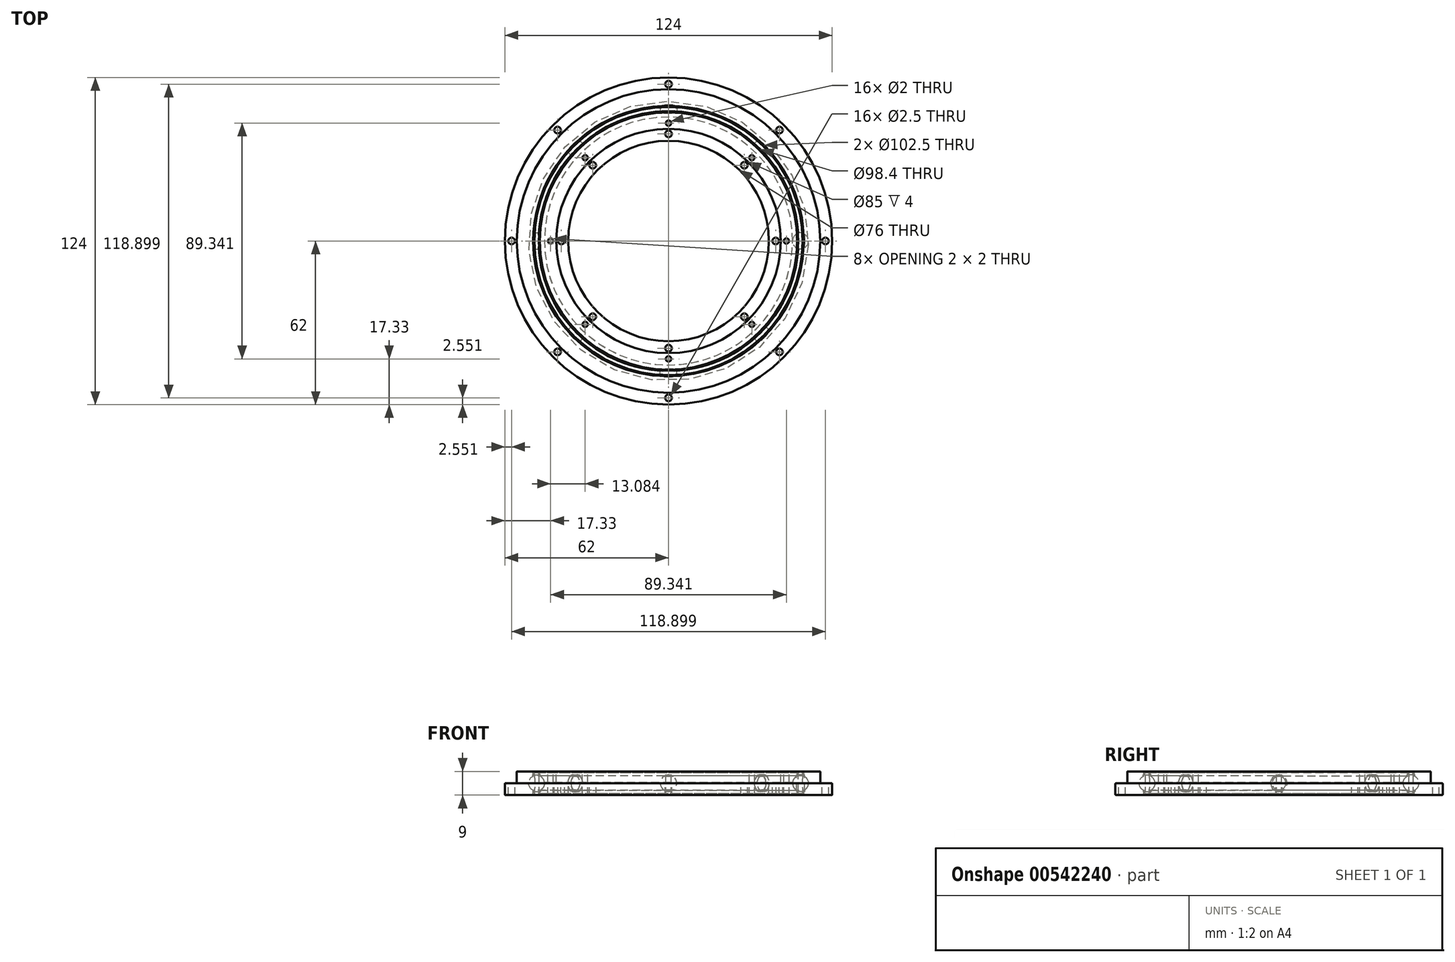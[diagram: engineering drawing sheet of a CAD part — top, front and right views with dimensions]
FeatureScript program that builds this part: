
annotation { "Feature Type Name" : "Feature", "Feature Type Description" : "" }
export const myFeature = defineFeature(function(context is Context, id is Id, definition is map)
    precondition{}
    {
        {
            var Q0;
            Q0=qCreatedBy(makeId("Front.planeOp"),FACE);
            var sketch = newSketch(context, id + "F0", { "sketchPlane" : qUnion([Q0])});
            skLineSegment(sketch, "E0", {"start": v(0, 5.1) * mm, "end": v(0, -5.34) * mm, "construction": true});
            skLineSegment(sketch, "E1", {"start": v(-106.53, 0) * mm, "end": v(60.8, 0) * mm, "construction": true});
            skLineSegment(sketch, "E2", {"start": v(50, 13.16) * mm, "end": v(50, -12.43) * mm, "construction": true});
            skCircle(sketch, "E3", {"center": v(50, 0) * mm, "radius": 3 * mm, "construction": true});
            skArc(sketch, "E4", {"start": v(51.25, 2.73) * mm, "mid": v(53, 0) * mm, "end": v(51.25, -2.73) * mm});
            skArc(sketch, "E5", {"start": v(48.75, 2.73) * mm, "mid": v(47, 0) * mm, "end": v(48.75, -2.73) * mm});
            skLineSegment(sketch, "E6", {"start": v(47.01, 0.25) * mm, "end": v(42.5, 0.25) * mm});
            skLineSegment(sketch, "E7", {"start": v(42.5, 0.25) * mm, "end": v(42.5, 4.5) * mm});
            skLineSegment(sketch, "E8", {"start": v(42.5, 4.5) * mm, "end": v(48.75, 4.5) * mm});
            skLineSegment(sketch, "E9", {"start": v(48.75, 4.5) * mm, "end": v(48.75, 2.73) * mm});
            skLineSegment(sketch, "E10", {"start": v(47, 0) * mm, "end": v(38, 0) * mm});
            skLineSegment(sketch, "E11", {"start": v(38, 0) * mm, "end": v(38, -4.5) * mm});
            skLineSegment(sketch, "E12", {"start": v(38, -4.5) * mm, "end": v(48.75, -4.5) * mm});
            skLineSegment(sketch, "E13", {"start": v(48.75, -4.5) * mm, "end": v(48.75, -2.73) * mm});
            skLineSegment(sketch, "E14", {"start": v(51.25, -2.73) * mm, "end": v(51.25, -4.5) * mm});
            skLineSegment(sketch, "E15", {"start": v(51.25, -4.5) * mm, "end": v(62, -4.5) * mm});
            skLineSegment(sketch, "E16", {"start": v(57.5, 0) * mm, "end": v(57.5, 4.5) * mm});
            skLineSegment(sketch, "E17", {"start": v(57.5, 4.5) * mm, "end": v(51.25, 4.5) * mm});
            skLineSegment(sketch, "E18", {"start": v(51.25, 4.5) * mm, "end": v(51.25, 2.73) * mm});
            skLineSegment(sketch, "E19", {"start": v(49.2, 4) * mm, "end": v(49.2, -4) * mm});
            skLineSegment(sketch, "E20", {"start": v(49.2, -4) * mm, "end": v(50.8, -4) * mm});
            skLineSegment(sketch, "E21", {"start": v(50.8, -4) * mm, "end": v(50.8, 4) * mm});
            skLineSegment(sketch, "E22", {"start": v(50.8, 4) * mm, "end": v(49.2, 4) * mm});
            skLineSegment(sketch, "E23", {"start": v(57.5, 0) * mm, "end": v(62, 0) * mm});
            skLineSegment(sketch, "E24", {"start": v(62, 0) * mm, "end": v(62, -4.5) * mm});
            skSolve(sketch);
        }
        {
            var Q0;
            Q0 = qSketchRegion(id + "F0", true);
            var Q1;
            Q1=sQuery(id+"F0.wireOp",EDGE,"E0");
            revolve(context, id + "F1", {"surfaceOperationType" : NewSurfaceOperationType.NEW, "entities" : qUnion([Q0]), "axis" : qUnion([Q1]), "revolveType" : RevolveType.FULL});
        }
        {
            var Q0;
            Q0=qCreatedBy(makeId("Front.planeOp"),FACE);
            var sketch = newSketch(context, id + "F2", { "sketchPlane" : qUnion([Q0])});
            skArc(sketch, "E25", {"start": v(50, 3) * mm, "mid": v(53, 0) * mm, "end": v(50, -3) * mm});
            skLineSegment(sketch, "E26", {"start": v(50, 3) * mm, "end": v(50, -3) * mm});
            skSolve(sketch);
        }
        {
            var Q0;
            Q0 = qSketchRegion(id + "F2", true);
            var Q1;
            Q1=sQuery(id+"F2.wireOp",EDGE,"E26");
            revolve(context, id + "F3", {"surfaceOperationType" : NewSurfaceOperationType.NEW, "entities" : qUnion([Q0]), "axis" : qUnion([Q1]), "revolveType" : RevolveType.FULL});
        }
        {
            assignVariable(context, id + "F4", {"name" : "num_balls", "anyValue" : 8});
        }
        {
            var Q0;
            Q0=qCreatedBy(makeId("Right.planeOp"),FACE);
            var Q1;
            Q1=sQuery(id+"F0.wireOp",VERTEX,"E3.center");
            cPlane(context, id + "F5", {"entities" : qUnion([Q0, Q1]), "cplaneType" : CPlaneType.PLANE_POINT, "offset" : 25 * mm, "width" : 150 * mm, "height" : 150 * mm});
        }
        {
            var Q0;
            Q0=qCreatedBy(id+"F5.planeOp",FACE);
            var sketch = newSketch(context, id + "F6", { "sketchPlane" : qUnion([Q0])});
            skCircle(sketch, "E27", {"center": v(0, 0) * mm, "radius": 3.12 * mm});
            skSolve(sketch);
        }
        {
            var Q0;
            Q0 = qSketchRegion(id + "F6", true);
            extrude(context, id + "F7", {"entities" : qUnion([Q0]), "endBound" : BoundingType.SYMMETRIC, "depth" : 3 * mm, "offsetDistance" : 25 * mm});
        }
        {
            var Q0;
            Q0=makeQuery(id+"F7.opExtrude","SWEPT_BODY",BODY,{"disambiguationData":[OSD([sQuery(id+"F6.wireOp",EDGE,"E27")])]});
            var Q1;
            Q1=sQuery(id+"F0.wireOp",EDGE,"E0");
            circularPattern(context, id + "F8", {"operationType" : NewBodyOperationType.REMOVE, "entities" : qUnion([Q0]), "axis" : qUnion([Q1]), "angle" : 360 * degree, "instanceCount" : getVariable(context, 'num_balls'), "equalSpace" : true});
        }
        {
            var Q0;
            Q0=makeQuery(id+"F1.opRevolve","SWEPT_FACE",FACE,{"disambiguationData":[OSD([sQuery(id+"F0.wireOp",EDGE,"E8")])]});
            var sketch = newSketch(context, id + "F9", { "sketchPlane" : qUnion([Q0])});
            skCircle(sketch, "E28", {"center": v(44.67, 0) * mm, "radius": 1 * mm});
            skCircle(sketch, "E29", {"center": v(40.6, 0) * mm, "radius": 1.25 * mm});
            skCircle(sketch, "E30", {"center": v(59.45, 0) * mm, "radius": 1.25 * mm});
            skCircle(sketch, "E31.1.0", {"center": v(28.71, 28.71) * mm, "radius": 1.25 * mm});
            skCircle(sketch, "E31.1.1", {"center": v(31.59, 31.59) * mm, "radius": 1 * mm});
            skCircle(sketch, "E31.1.2", {"center": v(42.04, 42.04) * mm, "radius": 1.25 * mm});
            skCircle(sketch, "E31.2.0", {"center": v(0, 40.6) * mm, "radius": 1.25 * mm});
            skCircle(sketch, "E31.2.1", {"center": v(0, 44.67) * mm, "radius": 1 * mm});
            skCircle(sketch, "E31.2.2", {"center": v(0, 59.45) * mm, "radius": 1.25 * mm});
            skPoint(sketch, "E31.center", {"position": v(0, 0) * mm});
            skCircle(sketch, "E32.1.3.0", {"center": v(-28.71, 28.71) * mm, "radius": 1.25 * mm});
            skCircle(sketch, "E32.2.3.0", {"center": v(-31.59, 31.59) * mm, "radius": 1 * mm});
            skCircle(sketch, "E32.4.3.0", {"center": v(-42.04, 42.04) * mm, "radius": 1.25 * mm});
            skCircle(sketch, "E32.1.4.0", {"center": v(-40.6, 0) * mm, "radius": 1.25 * mm});
            skCircle(sketch, "E32.2.4.0", {"center": v(-44.67, 0) * mm, "radius": 1 * mm});
            skCircle(sketch, "E32.4.4.0", {"center": v(-59.45, 0) * mm, "radius": 1.25 * mm});
            skCircle(sketch, "E32.1.5.0", {"center": v(-28.71, -28.71) * mm, "radius": 1.25 * mm});
            skCircle(sketch, "E32.2.5.0", {"center": v(-31.59, -31.59) * mm, "radius": 1 * mm});
            skCircle(sketch, "E32.4.5.0", {"center": v(-42.04, -42.04) * mm, "radius": 1.25 * mm});
            skCircle(sketch, "E32.1.6.0", {"center": v(0, -40.6) * mm, "radius": 1.25 * mm});
            skCircle(sketch, "E32.2.6.0", {"center": v(0, -44.67) * mm, "radius": 1 * mm});
            skCircle(sketch, "E32.4.6.0", {"center": v(0, -59.45) * mm, "radius": 1.25 * mm});
            skCircle(sketch, "E32.1.7.0", {"center": v(28.71, -28.71) * mm, "radius": 1.25 * mm});
            skCircle(sketch, "E32.2.7.0", {"center": v(31.59, -31.59) * mm, "radius": 1 * mm});
            skCircle(sketch, "E32.4.7.0", {"center": v(42.04, -42.04) * mm, "radius": 1.25 * mm});
            skSolve(sketch);
        }
        {
            var Q0;
            Q0 = qSketchRegion(id + "F9", true);
            extrude(context, id + "F10", {"entities" : qUnion([Q0]), "operationType" : NewBodyOperationType.REMOVE, "endBound" : BoundingType.THROUGH_ALL, "oppositeDirection" : true, "depth" : 25 * mm, "offsetDistance" : 25 * mm});
        }
        {
            var Q0;
            Q0=makeQuery(id+"F1.opRevolve","SWEPT_EDGE",EDGE,{"disambiguationData":[OSD([sQuery(id+"F0.wireOp",EDGE,"E16"),sQuery(id+"F0.wireOp",EDGE,"E23")])]});
            var Q1;
            Q1=makeQuery(id+"F1.opRevolve","SWEPT_EDGE",EDGE,{"disambiguationData":[OSD([sQuery(id+"F0.wireOp",EDGE,"E10"),sQuery(id+"F0.wireOp",EDGE,"E11")])]});
            var Q2;
            Q2=makeQuery(id+"F1.opRevolve","SWEPT_EDGE",EDGE,{"disambiguationData":[OSD([sQuery(id+"F0.wireOp",EDGE,"E7"),sQuery(id+"F0.wireOp",EDGE,"E8")])]});
            var Q3;
            Q3=makeQuery(id+"F1.opRevolve","SWEPT_FACE",FACE,{"disambiguationData":[OSD([sQuery(id+"F0.wireOp",EDGE,"E17")])]});
            var Q4;
            Q4=makeQuery(id+"F1.opRevolve","SWEPT_EDGE",EDGE,{"disambiguationData":[OSD([sQuery(id+"F0.wireOp",EDGE,"E16"),sQuery(id+"F0.wireOp",EDGE,"E17")])]});
            var Q5;
            Q5=makeQuery(id+"F1.opRevolve","SWEPT_EDGE",EDGE,{"disambiguationData":[OSD([sQuery(id+"F0.wireOp",EDGE,"E23"),sQuery(id+"F0.wireOp",EDGE,"E24")])]});
            var Q6;
            Q6=makeQuery(id+"F1.opRevolve","SWEPT_EDGE",EDGE,{"disambiguationData":[OSD([sQuery(id+"F0.wireOp",EDGE,"E19"),sQuery(id+"F0.wireOp",EDGE,"E22")])]});
            var Q7;
            Q7=makeQuery(id+"F1.opRevolve","SWEPT_EDGE",EDGE,{"disambiguationData":[OSD([sQuery(id+"F0.wireOp",EDGE,"E21"),sQuery(id+"F0.wireOp",EDGE,"E22")])]});
            var Q8;
            Q8=makeQuery(id+"F1.opRevolve","SWEPT_EDGE",EDGE,{"disambiguationData":[OSD([sQuery(id+"F0.wireOp",EDGE,"E11"),sQuery(id+"F0.wireOp",EDGE,"E12")])]});
            var Q9;
            Q9=makeQuery(id+"F1.opRevolve","SWEPT_EDGE",EDGE,{"disambiguationData":[OSD([sQuery(id+"F0.wireOp",EDGE,"E12"),sQuery(id+"F0.wireOp",EDGE,"E13")])]});
            var Q10;
            Q10=makeQuery(id+"F1.opRevolve","SWEPT_EDGE",EDGE,{"disambiguationData":[OSD([sQuery(id+"F0.wireOp",EDGE,"E19"),sQuery(id+"F0.wireOp",EDGE,"E20")])]});
            var Q11;
            Q11=makeQuery(id+"F1.opRevolve","SWEPT_EDGE",EDGE,{"disambiguationData":[OSD([sQuery(id+"F0.wireOp",EDGE,"E20"),sQuery(id+"F0.wireOp",EDGE,"E21")])]});
            var Q12;
            Q12=makeQuery(id+"F1.opRevolve","SWEPT_EDGE",EDGE,{"disambiguationData":[OSD([sQuery(id+"F0.wireOp",EDGE,"E14"),sQuery(id+"F0.wireOp",EDGE,"E15")])]});
            var Q13;
            Q13=makeQuery(id+"F1.opRevolve","SWEPT_EDGE",EDGE,{"disambiguationData":[OSD([sQuery(id+"F0.wireOp",EDGE,"E15"),sQuery(id+"F0.wireOp",EDGE,"E24")])]});
            fillet(context, id + "F11", {"entities" : qUnion([Q0, Q1, Q2, Q3, Q4, Q5, Q6, Q7, Q8, Q9, Q10, Q11, Q12, Q13]), "radius" : 0.25 * mm, "tangentPropagation" : true, "allowEdgeOverflow" : false});
        }
    });
